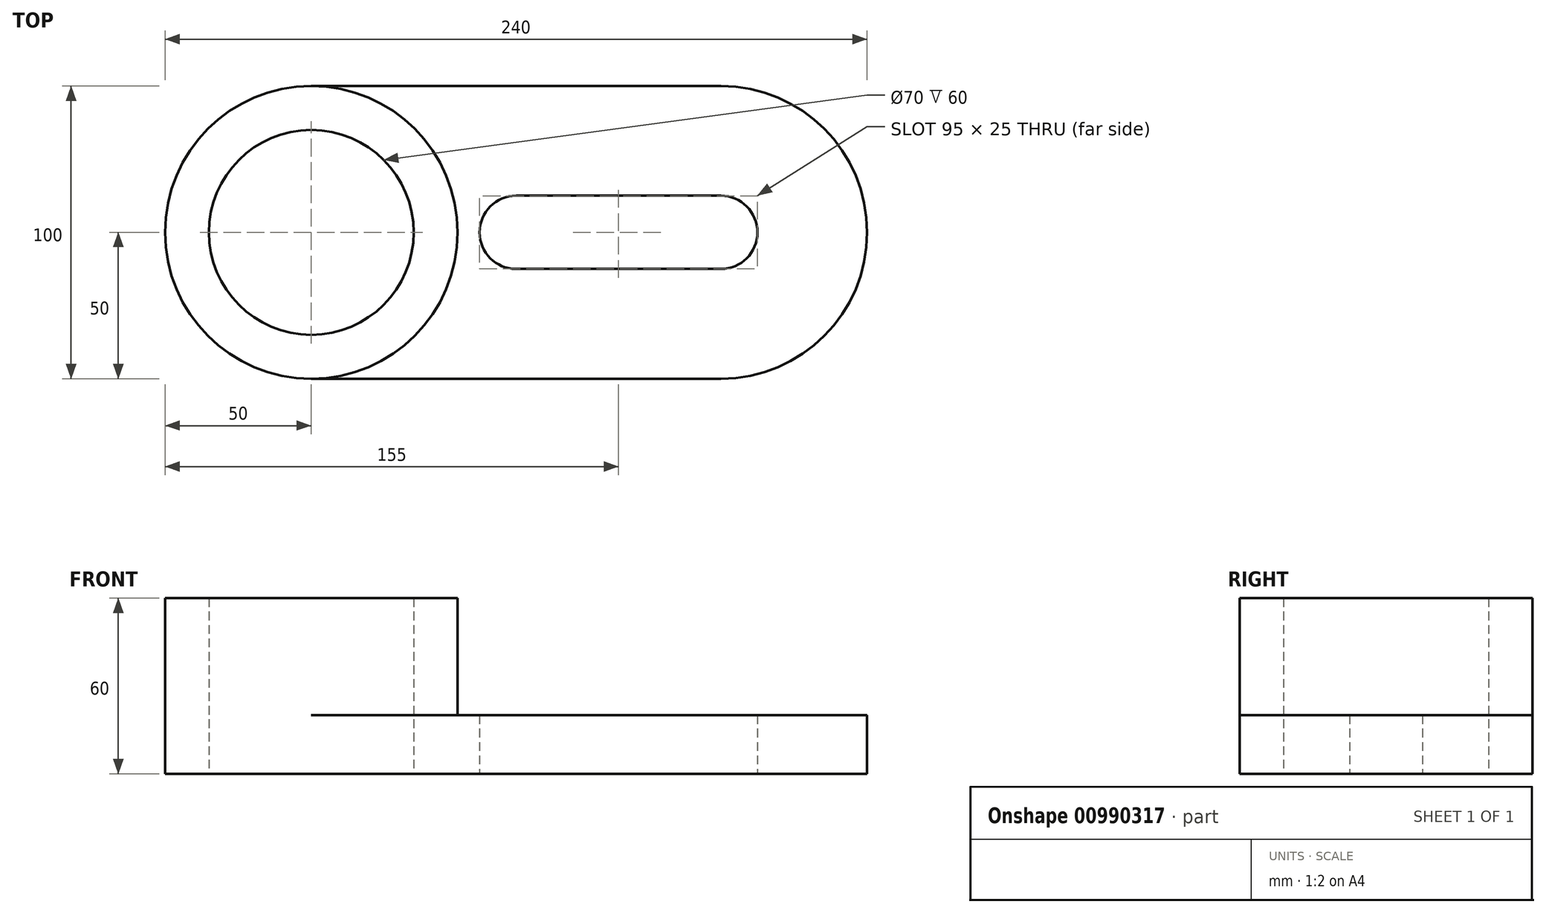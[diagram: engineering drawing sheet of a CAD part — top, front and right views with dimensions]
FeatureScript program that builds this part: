
annotation { "Feature Type Name" : "Feature", "Feature Type Description" : "" }
export const myFeature = defineFeature(function(context is Context, id is Id, definition is map)
    precondition{}
    {
        {
            var Q0;
            Q0=qCreatedBy(makeId("Top.planeOp"),FACE);
            var sketch = newSketch(context, id + "F0", { "sketchPlane" : qUnion([Q0])});
            skLineSegment(sketch, "E0", {"start": v(0, 0) * mm, "end": v(70, 0) * mm, "construction": true});
            skLineSegment(sketch, "E1.MirrorCS", {"start": v(0, 0) * mm, "end": v(-70, 0) * mm, "construction": true});
            skLineSegment(sketch, "E2", {"start": v(0, -12.5) * mm, "end": v(70, -12.5) * mm});
            skLineSegment(sketch, "E3.MirrorCS", {"start": v(0, 12.5) * mm, "end": v(70, 12.5) * mm});
            skCircle(sketch, "E4", {"center": v(-70, 0) * mm, "radius": 50 * mm});
            skLineSegment(sketch, "E5", {"start": v(-70, 0) * mm, "end": v(-70, -50) * mm, "construction": true});
            skLineSegment(sketch, "E6", {"start": v(-70, -50) * mm, "end": v(70, -50) * mm});
            skLineSegment(sketch, "E7.MirrorCS", {"start": v(-70, 50) * mm, "end": v(70, 50) * mm});
            skCircle(sketch, "E8", {"center": v(-70, 0) * mm, "radius": 35 * mm});
            skArc(sketch, "E9", {"start": v(70, -12.5) * mm, "mid": v(82.5, 0) * mm, "end": v(70, 12.5) * mm});
            skArc(sketch, "E10", {"start": v(0, 12.5) * mm, "mid": v(-12.5, 0) * mm, "end": v(0, -12.5) * mm});
            skArc(sketch, "E11", {"start": v(70, 50) * mm, "mid": v(120, 0) * mm, "end": v(70, -50) * mm});
            skSolve(sketch);
        }
        {
            var Q0;
            Q0=makeQuery(id+"F0.imprint","IMPRINT",FACE,{"disambiguationData":[TD([[makeQuery(id+"F0.imprint","IMPRINT",EDGE,{"derivedFrom":sQuery(id+"F0.wireOp",EDGE,"E8")}),-1.0]])]});
            var Q1;
            Q1=makeQuery(id+"F0.imprint","IMPRINT",FACE,{"disambiguationData":[TD([[makeQuery(id+"F0.imprint","IMPRINT",EDGE,{"derivedFrom":sQuery(id+"F0.wireOp",EDGE,"E2")}),-1.0]])]});
            extrude(context, id + "F1", {"entities" : qUnion([Q0, Q1]), "depth" : 20 * mm, "offsetDistance" : 25 * mm});
        }
        {
            var Q0;
            Q0=makeQuery(id+"F0.imprint","IMPRINT",FACE,{"disambiguationData":[TD([[makeQuery(id+"F0.imprint","IMPRINT",EDGE,{"derivedFrom":sQuery(id+"F0.wireOp",EDGE,"E8")}),-1.0]])]});
            extrude(context, id + "F2", {"entities" : qUnion([Q0]), "operationType" : NewBodyOperationType.ADD, "depth" : 60 * mm, "offsetDistance" : 25 * mm});
        }
    });
